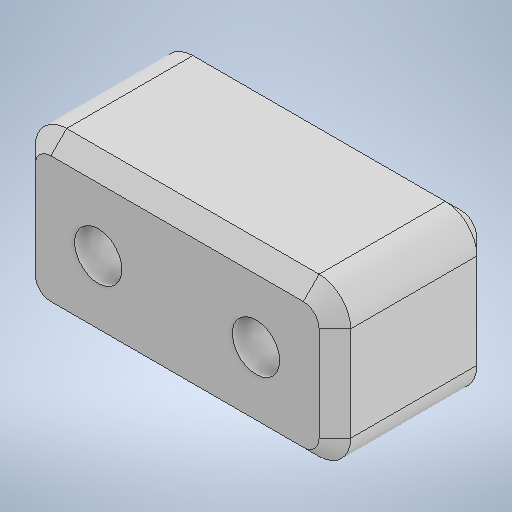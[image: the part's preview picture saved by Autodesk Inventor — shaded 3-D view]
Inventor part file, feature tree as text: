
AUTODESK INVENTOR PART (.ipt)
format: ipt  version: 2025.3 (Build 293356000, 356)  size: 530,432 bytes
history: native  units: mm
features: other x1, extrude x1, fillet x1, chamfer x1, sketch x1
ambient origin geometry x8: Origin, YZ Plane, XZ Plane, XY Plane, X Axis, Y Axis, Z Axis, Center Point
bodies: Body1 (feature_tree)
feature tree (5):
  other  "솔리드1"
  extrude  "돌출1"  Depth=10.0mm
  fillet  "모깎기1"  Radius=20.0mm
  chamfer  "모따기1"  Distance=3.0mm
  sketch  "스케치1"
